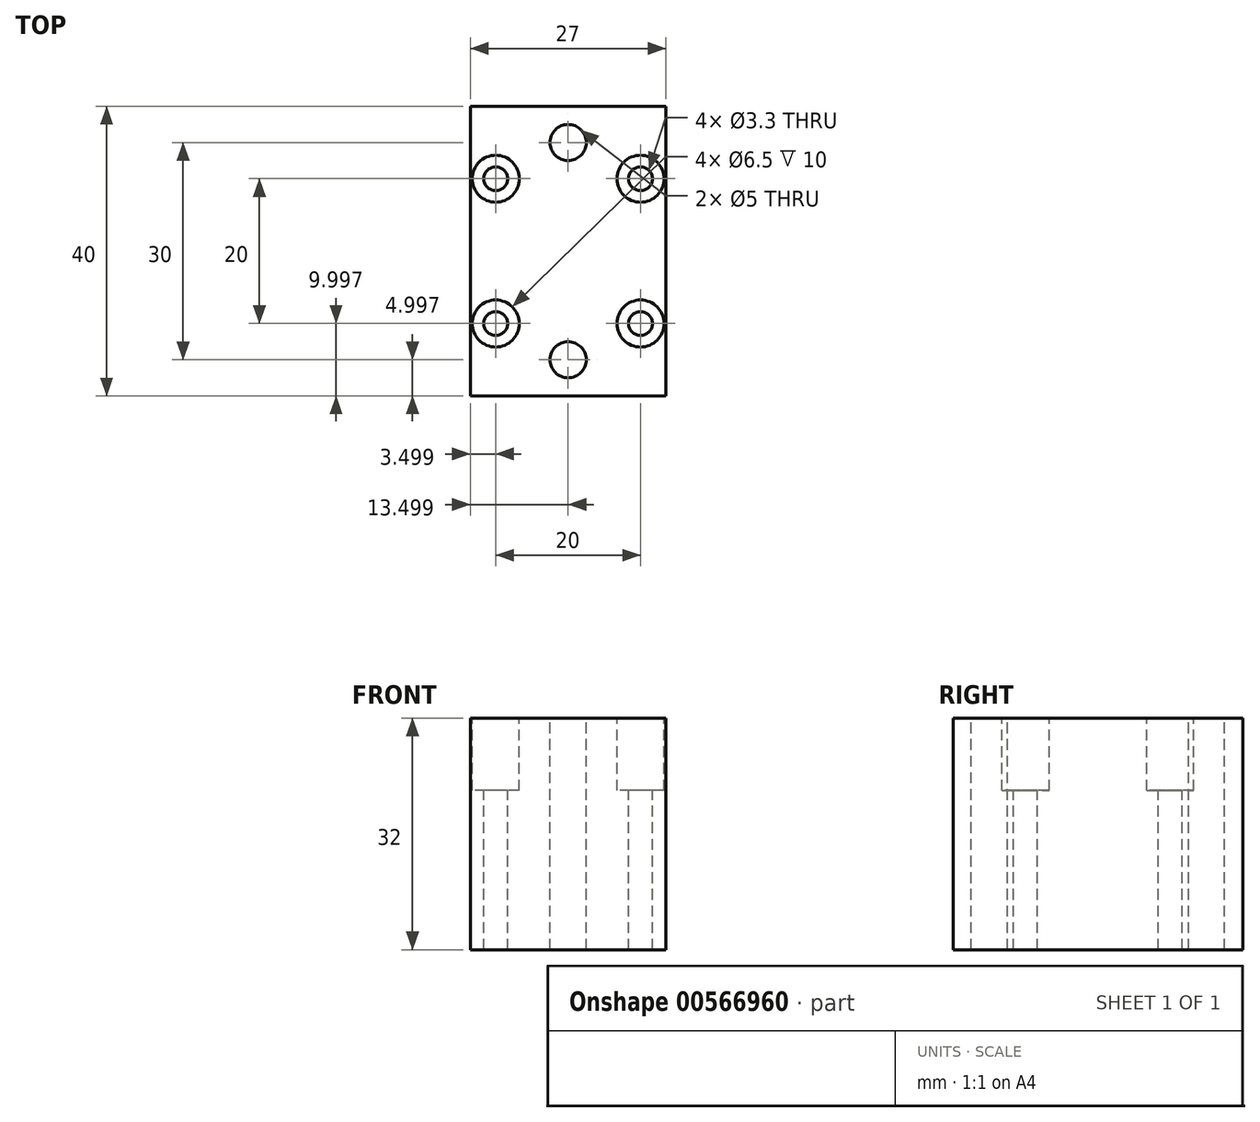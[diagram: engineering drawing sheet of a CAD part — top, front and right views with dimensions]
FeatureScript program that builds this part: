
annotation { "Feature Type Name" : "Feature", "Feature Type Description" : "" }
export const myFeature = defineFeature(function(context is Context, id is Id, definition is map)
    precondition{}
    {
        {
            var Q0;
            Q0=qCreatedBy(makeId("Top.planeOp"),FACE);
            var sketch = newSketch(context, id + "F0", { "sketchPlane" : qUnion([Q0])});
            skLineSegment(sketch, "E0.bottom", {"start": v(-36.8, -23.83) * mm, "end": v(-9.8, -23.83) * mm});
            skLineSegment(sketch, "E0.top", {"start": v(-36.8, -63.83) * mm, "end": v(-9.8, -63.83) * mm});
            skLineSegment(sketch, "E0.left", {"start": v(-36.8, -23.83) * mm, "end": v(-36.8, -63.83) * mm});
            skLineSegment(sketch, "E0.right", {"start": v(-9.8, -23.83) * mm, "end": v(-9.8, -63.83) * mm});
            skSolve(sketch);
        }
        {
            var Q0;
            Q0=makeQuery(id+"F0.imprint","IMPRINT",FACE,{"disambiguationData":[TD([[makeQuery(id+"F0.imprint","IMPRINT",EDGE,{"derivedFrom":sQuery(id+"F0.wireOp",EDGE,"E0.bottom")}),-1.0]])]});
            extrude(context, id + "F1", {"entities" : qUnion([Q0]), "depth" : 32 * mm});
        }
        {
            var Q0;
            Q0=makeQuery(id+"F1.opExtrude","CAP_FACE",FACE,{"disambiguationData":[OSD([sQuery(id+"F0.wireOp",EDGE,"E0.bottom"),sQuery(id+"F0.wireOp",EDGE,"E0.top"),sQuery(id+"F0.wireOp",EDGE,"E0.left"),sQuery(id+"F0.wireOp",EDGE,"E0.right")])],"isStart":false});
            var sketch = newSketch(context, id + "F2", { "sketchPlane" : qUnion([Q0])});
            skLineSegment(sketch, "E1", {"start": v(-23.3, -23.83) * mm, "end": v(-23.3, -63.83) * mm, "construction": true});
            skLineSegment(sketch, "E2", {"start": v(-36.8, -43.83) * mm, "end": v(-9.8, -43.83) * mm, "construction": true});
            skLineSegment(sketch, "E3.top", {"start": v(-23.3, -33.83) * mm, "end": v(-33.3, -33.83) * mm, "construction": true});
            skLineSegment(sketch, "E3.right", {"start": v(-33.3, -43.83) * mm, "end": v(-33.3, -33.83) * mm, "construction": true});
            skLineSegment(sketch, "E4.MirrorCS", {"start": v(-23.3, -33.83) * mm, "end": v(-13.3, -33.83) * mm, "construction": true});
            skLineSegment(sketch, "E5.MirrorCS", {"start": v(-13.3, -43.83) * mm, "end": v(-13.3, -33.83) * mm, "construction": true});
            skLineSegment(sketch, "E6.MirrorCS", {"start": v(-13.3, -43.83) * mm, "end": v(-13.3, -53.83) * mm, "construction": true});
            skLineSegment(sketch, "E7.MirrorCS", {"start": v(-23.3, -53.83) * mm, "end": v(-13.3, -53.83) * mm, "construction": true});
            skLineSegment(sketch, "E8.MirrorCS", {"start": v(-23.3, -53.83) * mm, "end": v(-33.3, -53.83) * mm, "construction": true});
            skLineSegment(sketch, "E9.MirrorCS", {"start": v(-33.3, -43.83) * mm, "end": v(-33.3, -53.83) * mm, "construction": true});
            skPoint(sketch, "E10", {"position": v(-23.3, -28.83) * mm});
            skPoint(sketch, "E11.MirrorP", {"position": v(-23.3, -58.83) * mm});
            skSolve(sketch);
        }
        {
            var Q0;
            Q0=sQuery(id+"F2.wireOp",VERTEX,"E3.top.end");
            var Q1;
            Q1=sQuery(id+"F2.wireOp",VERTEX,"E5.MirrorCS.end");
            var Q2;
            Q2=sQuery(id+"F2.wireOp",VERTEX,"E6.MirrorCS.end");
            var Q3;
            Q3=sQuery(id+"F2.wireOp",VERTEX,"E8.MirrorCS.end");
            var Q4;
            Q4=makeQuery(id+"F1.opExtrude","SWEPT_BODY",BODY,{"disambiguationData":[OSD([sQuery(id+"F0.wireOp",EDGE,"E0.bottom"),sQuery(id+"F0.wireOp",EDGE,"E0.top"),sQuery(id+"F0.wireOp",EDGE,"E0.left"),sQuery(id+"F0.wireOp",EDGE,"E0.right")])]});
            hole(context, id + "F3", {"style" : HoleStyle.C_BORE, "endStyle" : HoleEndStyle.THROUGH, "holeDiameter" : 3.3 * mm, "cBoreDiameter" : 6.5 * mm, "cBoreDepth" : 10 * mm, "locations" : qUnion([Q0, Q1, Q2, Q3]), "scope" : qUnion([Q4]), "tappedDepth" : 12 * mm, "tapClearance" : 3});
        }
        {
            var Q0;
            Q0=sQuery(id+"F2.wireOp",VERTEX,"E10");
            var Q1;
            Q1=sQuery(id+"F2.wireOp",VERTEX,"E11.MirrorP");
            var Q2;
            Q2=makeQuery(id+"F1.opExtrude","SWEPT_BODY",BODY,{"disambiguationData":[OSD([sQuery(id+"F0.wireOp",EDGE,"E0.bottom"),sQuery(id+"F0.wireOp",EDGE,"E0.top"),sQuery(id+"F0.wireOp",EDGE,"E0.left"),sQuery(id+"F0.wireOp",EDGE,"E0.right")])]});
            hole(context, id + "F4", {"style" : HoleStyle.SIMPLE, "endStyle" : HoleEndStyle.THROUGH, "standardTappedOrClearance" : lookupTablePath({ "standard" : "ISO", "engagement" : "75%", "pitch" : "1 mm", "size" : "M6", "type" : "Tapped" }), "standardBlindInLast" : lookupTablePath({ "standard" : "ISO", "engagement" : "75%", "pitch" : "1 mm", "size" : "M6", "type" : "Tapped" }), "holeDiameter" : 5 * mm, "locations" : qUnion([Q0, Q1]), "scope" : qUnion([Q2]), "isTappedThrough" : true, "majorDiameter" : 6 * mm, "showTappedDepth" : true});
        }
    });
